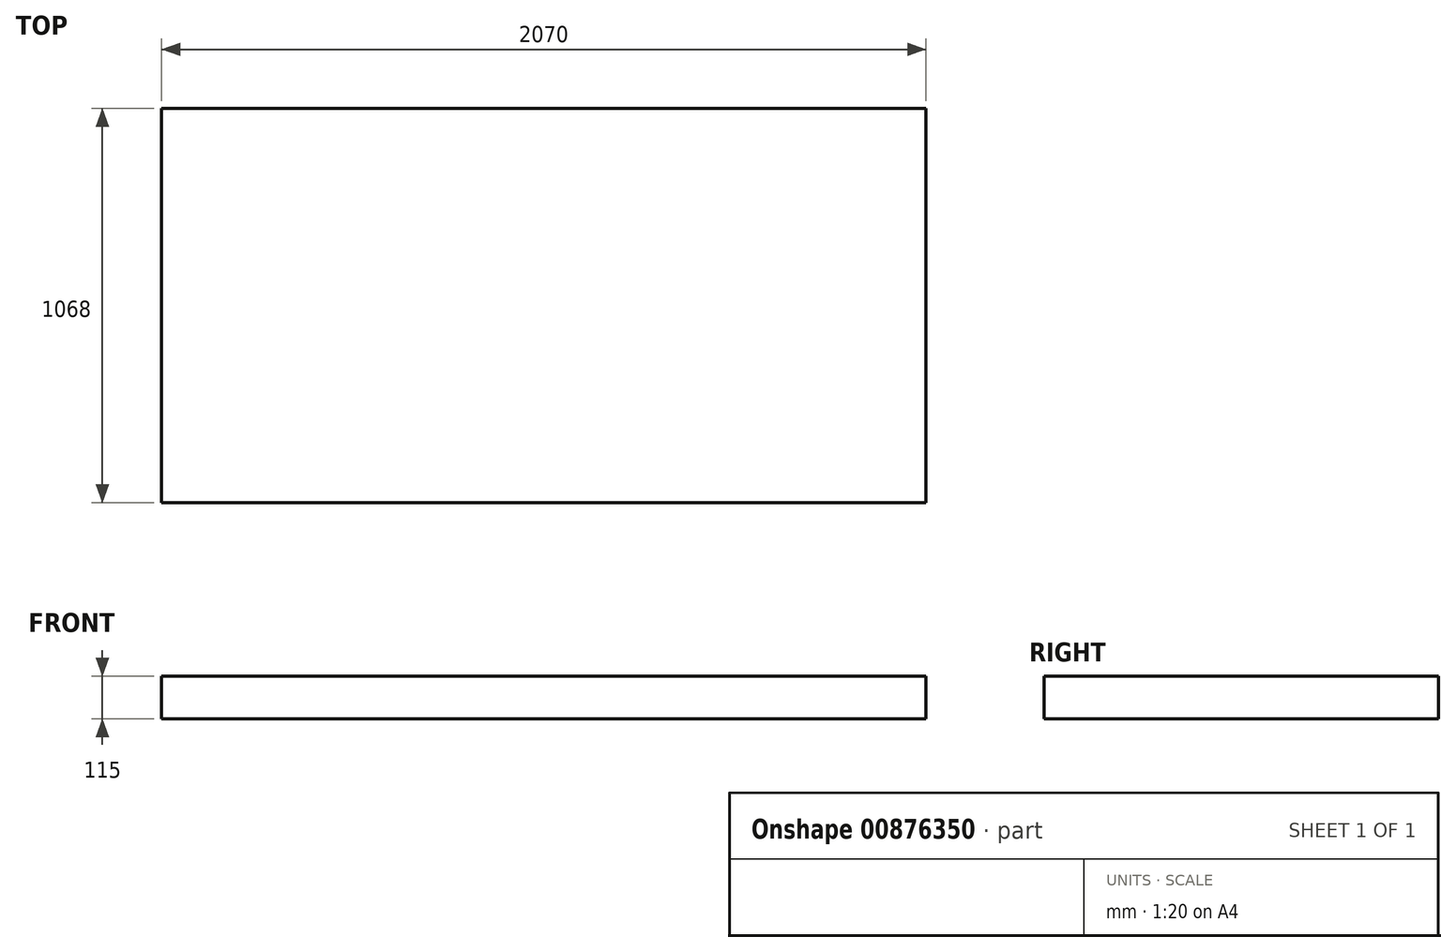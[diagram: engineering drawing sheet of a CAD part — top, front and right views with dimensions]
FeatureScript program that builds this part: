
annotation { "Feature Type Name" : "Feature", "Feature Type Description" : "" }
export const myFeature = defineFeature(function(context is Context, id is Id, definition is map)
    precondition{}
    {
        {
            var Q0;
            Q0=qCreatedBy(makeId("Top.planeOp"),FACE);
            var sketch = newSketch(context, id + "F0", { "sketchPlane" : qUnion([Q0])});
            skLineSegment(sketch, "E0.bottom", {"start": v(1035, 534) * mm, "end": v(-1035, 534) * mm});
            skLineSegment(sketch, "E0.top", {"start": v(1035, -534) * mm, "end": v(-1035, -534) * mm});
            skLineSegment(sketch, "E0.left", {"start": v(1035, 534) * mm, "end": v(1035, -534) * mm});
            skLineSegment(sketch, "E0.right", {"start": v(-1035, 534) * mm, "end": v(-1035, -534) * mm});
            skPoint(sketch, "E0.middle", {"position": v(0, 0) * mm});
            skSolve(sketch);
        }
        {
            var Q0;
            Q0=makeQuery(id+"F0.imprint","IMPRINT",FACE,{"disambiguationData":[TD([[makeQuery(id+"F0.imprint","IMPRINT",EDGE,{"derivedFrom":sQuery(id+"F0.wireOp",EDGE,"E0.bottom")}),1.0]])]});
            extrude(context, id + "F1", {"entities" : qUnion([Q0]), "depth" : 115 * mm, "offsetDistance" : 25 * mm});
        }
    });
